# Revit family: LBA6
name_source: partatom
category: Equipement spécialisé
revit_build: Autodesk Revit 2017 (Build: 20160225_1515(x64)
units: mm (PartAtom-declared; Revit-internal decimal feet)

## family parameters
Basée sur le plan de construction = Non
Cote de connecteur circulaire = Utiliser le diamètre
Couper avec des vides une fois chargée = Non
Partagée = Non
Point de calcul de pièce = Non
Toujours verticalement = Oui
Type d'élément = Normal

## types (3) — shared parameters
Fabricant = La Barrière Automatique
URL = https://barriere-automatique.com
diamètre_bareau_GA = 25 mm  [stored 0.082021 ft]
diamètre_grillage_GA = 15 mm  [stored 0.0492126 ft]
distance lisse du borne = 225 mm  [stored 0.738189 ft]
epaisseur_repose_barrière_V = 100 mm  [stored 0.328084 ft]
h_axe_chapeau = 112 mm  [stored 0.367454 ft]
h_chapeau = 916 mm
largeur_borne = 360 mm  [stored 1.1811 ft]
largeur_chapeau = 365 mm  [stored 1.19751 ft]
longueur_borne = 360 mm  [stored 1.1811 ft]
longueur_chapeau = 365 mm  [stored 1.19751 ft]
matériau_borne = Stratifié, bleu marine
matériau_chapeau = BLANC_MAT
matériau_lisse = BLANC_MAT
matériau_repos_barrière = POSTE SUPPORT
origine_GA = 150 mm

## per-type parameters (varying)
| type | Modèle | Nombre_barreaux_GA | Visibilité_Grillage_GA | Visibilité_Support | distance_entre_grilles_GA | décalage sous lisse_GA | entreaxe_massifs | epaisseur_lisse | h_GA | h_repose_barrière | hauteur_lisse | longueur_GA | longueur_lisse | longueur_lisse_attaché au borne | position_grille1_GA |
| LBA6_lise_ovale 4000mm | LBA 6 | 8 | Non | Non | 390 mm  [stored 1.27953 ft] | 104 mm | 3750 mm  [stored 12.3031 ft] | 57 mm  [stored 0.187008 ft] | 728 mm  [stored 2.38845 ft] | 832 mm | 84 mm  [stored 0.275591 ft] | 3700 mm  [stored 12.1391 ft] | 4000 mm  [stored 13.1234 ft] | 150 mm | 200 mm  [stored 0.656168 ft] |
| LBA6_lisse_ovale_GA | LBA 6 GA | 9 | Oui | Oui | 355 mm | 80 mm  [stored 0.262467 ft] | 3750 mm  [stored 12.3031 ft] | 50 mm  [stored 0.164042 ft] | 776 mm | 856 mm  [stored 2.8084 ft] | 60 mm  [stored 0.19685 ft] | 3700 mm  [stored 12.1391 ft] | 4000 mm  [stored 13.1234 ft] | 150 mm | 200 mm  [stored 0.656168 ft] |
| LBA6_lise_ovale 6000mm | LBA 6 | 13 | Non | Oui | 355 mm | 104 mm | 5800 mm | 57 mm  [stored 0.187008 ft] | 728 mm  [stored 2.38845 ft] | 832 mm | 84 mm  [stored 0.275591 ft] | 5750 mm | 6000 mm  [stored 19.685 ft] | 128 mm | 178 mm |

note: [stored X ft] marks values corroborated as IEEE doubles in the binary element streams (Revit-internal decimal feet)
